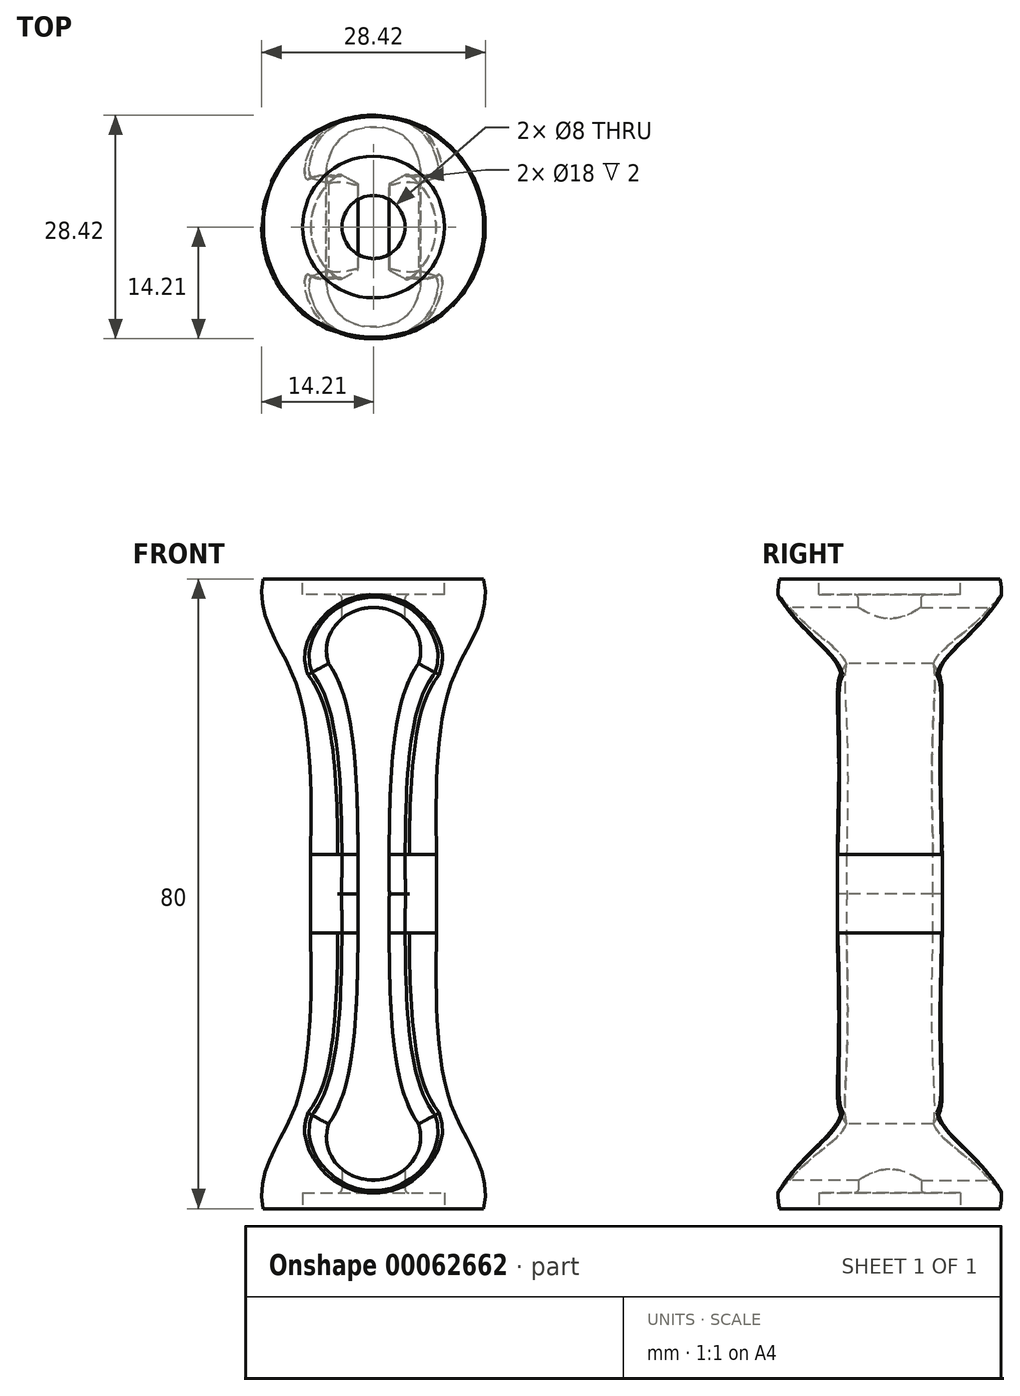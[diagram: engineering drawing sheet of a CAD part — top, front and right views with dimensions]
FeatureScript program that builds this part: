
annotation { "Feature Type Name" : "Feature", "Feature Type Description" : "" }
export const myFeature = defineFeature(function(context is Context, id is Id, definition is map)
    precondition{}
    {
        {
            var Q0;
            Q0=qCreatedBy(makeId("Front.planeOp"),FACE);
            var sketch = newSketch(context, id + "F0", { "sketchPlane" : qUnion([Q0])});
            skLineSegment(sketch, "E0", {"start": v(0, 0) * mm, "end": v(0, 40) * mm});
            skLineSegment(sketch, "E1", {"start": v(0, 40) * mm, "end": v(-14, 40) * mm});
            skLineSegment(sketch, "E2", {"start": v(0, 0) * mm, "end": v(-8, 0) * mm});
            skLineSegment(sketch, "E3", {"start": v(-8, 0) * mm, "end": v(-8, 5) * mm});
            skFitSpline(sketch, "E4", {"points": [v(-14, 40) * mm, v(-9.89, 26.85) * mm, v(-8, 5) * mm], "startDerivative": vector(-7.29, -34.58) * mm, "endDerivative": vector(-0.37, -33.72) * mm});
            skLineSegment(sketch, "E5.MirrorCS", {"start": v(-8, 0) * mm, "end": v(-8, -5) * mm});
            skLineSegment(sketch, "E6.MirrorCS", {"start": v(0, -40) * mm, "end": v(-14, -40) * mm});
            skLineSegment(sketch, "E7.MirrorCS", {"start": v(0, 0) * mm, "end": v(0, -40) * mm});
            skFitSpline(sketch, "E8.MirrorCS", {"points": [v(-14, -40) * mm, v(-9.89, -26.85) * mm, v(-8, -5) * mm], "startDerivative": vector(-7.29, 34.58) * mm, "endDerivative": vector(-0.37, 33.72) * mm});
            skSolve(sketch);
        }
        {
            var Q0;
            Q0 = qSketchRegion(id + "F0", true);
            var Q1;
            Q1=sQuery(id+"F0.wireOp",EDGE,"E7.MirrorCS");
            revolve(context, id + "F1", {"entities" : qUnion([Q0]), "axis" : qUnion([Q1]), "revolveType" : RevolveType.FULL});
        }
        {
            var Q0;
            Q0=makeQuery(id+"F1.opRevolve","SWEPT_FACE",FACE,{"disambiguationData":[OSD([sQuery(id+"F0.wireOp",EDGE,"E6.MirrorCS")])]});
            var sketch = newSketch(context, id + "F2", { "sketchPlane" : qUnion([Q0])});
            skCircle(sketch, "E9", {"center": v(0, 0) * mm, "radius": 4 * mm});
            skSolve(sketch);
        }
        {
            var Q0;
            Q0 = qSketchRegion(id + "F2", true);
            extrude(context, id + "F3", {"entities" : qUnion([Q0]), "operationType" : NewBodyOperationType.REMOVE, "oppositeDirection" : true, "depth" : 10 * mm});
        }
        {
            var Q0;
            Q0=qCreatedBy(makeId("Front.planeOp"),FACE);
            var sketch = newSketch(context, id + "F4", { "sketchPlane" : qUnion([Q0])});
            skLineSegment(sketch, "E10", {"start": v(0, 0) * mm, "end": v(0, 30.88) * mm});
            skLineSegment(sketch, "E11", {"start": v(2, 0) * mm, "end": v(-2, 0) * mm});
            skEllipticalArc(sketch, "E12", {});
            skFitSpline(sketch, "E13", {"points": [v(2, 0) * mm, v(5.72, 29.23) * mm, v(14.35, 33.66) * mm], "startDerivative": vector(-0.3, 57.22) * mm, "endDerivative": vector(24.53, 8.63) * mm});
            skLineSegment(sketch, "E14", {"start": v(0, 36.38) * mm, "end": v(0, 30.88) * mm});
            skEllipticalArc(sketch, "E15.MirrorCS", {});
            skFitSpline(sketch, "E16.MirrorCS", {"points": [v(-2, 0) * mm, v(-5.72, 29.23) * mm, v(-14.35, 33.66) * mm], "startDerivative": vector(0.3, 57.22) * mm, "endDerivative": vector(-24.53, 8.63) * mm});
            skFitSpline(sketch, "E17.MirrorCS", {"points": [v(2, 0) * mm, v(5.72, -29.23) * mm, v(14.35, -33.66) * mm], "startDerivative": vector(-0.3, -57.22) * mm, "endDerivative": vector(24.53, -8.63) * mm});
            skFitSpline(sketch, "E18.MirrorCS", {"points": [v(-2, 0) * mm, v(-5.72, -29.23) * mm, v(-14.35, -33.66) * mm], "startDerivative": vector(0.3, -57.22) * mm, "endDerivative": vector(-24.53, -8.63) * mm});
            skEllipticalArc(sketch, "E19.MirrorCS", {});
            skEllipticalArc(sketch, "E20.MirrorCS", {});
            const initialGuessF4  = {"E12": [0, 0.030878746884994077, 1, 0, 0.006, 0.0055, 5.978786873267516, 1.5707963267948966], "E15.MirrorCS": [0, 0.030878746884994077, -1, 0, 0.006, 0.0055, 4.71238898038469, 0.304398433912071], "E19.MirrorCS": [0, -0.030878746884994077, -1, 0, 0.006, 0.0055, 5.978786873267516, 1.5707963267948966], "E20.MirrorCS": [0, -0.030878746884994077, 1, 0, 0.006, 0.0055, 4.71238898038469, 0.3043984339120717]};
            skSetInitialGuess(sketch, initialGuessF4);
            skSolve(sketch);
        }
        {
            var Q0;
            Q0 = qSketchRegion(id + "F4", true);
            extrude(context, id + "F5", {"entities" : qUnion([Q0]), "operationType" : NewBodyOperationType.REMOVE, "endBound" : BoundingType.THROUGH_ALL, "oppositeDirection" : true, "depth" : 25 * mm, "hasSecondDirection" : true, "secondDirectionOppositeDirection" : false, "secondDirectionDepth" : 25 * mm});
        }
        {
            var Q0;
            Q0=makeQuery(id+"F1.opRevolve","SWEPT_FACE",FACE,{"disambiguationData":[OSD([sQuery(id+"F0.wireOp",EDGE,"E1")])]});
            var sketch = newSketch(context, id + "F6", { "sketchPlane" : qUnion([Q0])});
            skCircle(sketch, "E21", {"center": v(0, 0) * mm, "radius": 4 * mm});
            skSolve(sketch);
        }
        {
            var Q0;
            Q0 = qSketchRegion(id + "F6", true);
            extrude(context, id + "F7", {"entities" : qUnion([Q0]), "operationType" : NewBodyOperationType.REMOVE, "oppositeDirection" : true, "depth" : 10 * mm});
        }
        {
            var Q0;
            Q0=makeQuery(id+"F1.opRevolve","SWEPT_FACE",FACE,{"disambiguationData":[OSD([sQuery(id+"F0.wireOp",EDGE,"E6.MirrorCS")])]});
            var sketch = newSketch(context, id + "F8", { "sketchPlane" : qUnion([Q0])});
            skCircle(sketch, "E22", {"center": v(0, 0) * mm, "radius": 9 * mm});
            skSolve(sketch);
        }
        {
            var Q0;
            Q0 = qSketchRegion(id + "F8", true);
            extrude(context, id + "F9", {"entities" : qUnion([Q0]), "operationType" : NewBodyOperationType.REMOVE, "oppositeDirection" : true, "depth" : 2 * mm});
        }
        {
            var Q0;
            Q0=makeQuery(id+"F1.opRevolve","SWEPT_FACE",FACE,{"disambiguationData":[OSD([sQuery(id+"F0.wireOp",EDGE,"E1")])]});
            var sketch = newSketch(context, id + "F10", { "sketchPlane" : qUnion([Q0])});
            skCircle(sketch, "E23", {"center": v(0, 0) * mm, "radius": 9 * mm});
            skSolve(sketch);
        }
        {
            var Q0;
            Q0 = qSketchRegion(id + "F10", true);
            extrude(context, id + "F11", {"entities" : qUnion([Q0]), "operationType" : NewBodyOperationType.REMOVE, "oppositeDirection" : true, "depth" : 2 * mm});
        }
        {
            var Q0;
            Q0=makeQuery(id+"F5.boolean.opBoolean","INTERSECT",EDGE,{"disambiguationData":[OD(1.0)],"derivedFrom":[makeQuery(id+"F1.opRevolve","SWEPT_FACE",FACE,{"disambiguationData":[OSD([sQuery(id+"F0.wireOp",EDGE,"E8.MirrorCS")])]}),makeQuery(id+"F5.opExtrude","SWEPT_FACE",FACE,{"disambiguationData":[OSD([sQuery(id+"F4.wireOp",EDGE,"E19.MirrorCS"),sQuery(id+"F4.wireOp",EDGE,"E20.MirrorCS")])]})]});
            var Q1;
            Q1=makeQuery(id+"F5.boolean.opBoolean","INTERSECT",EDGE,{"disambiguationData":[OD(1.0)],"derivedFrom":[makeQuery(id+"F1.opRevolve","SWEPT_FACE",FACE,{"disambiguationData":[OSD([sQuery(id+"F0.wireOp",EDGE,"E8.MirrorCS")])]}),makeQuery(id+"F5.opExtrude","SWEPT_FACE",FACE,{"disambiguationData":[OSD([sQuery(id+"F4.wireOp",EDGE,"E17.MirrorCS")])]})]});
            var Q2;
            Q2=makeQuery(id+"F5.boolean.opBoolean","INTERSECT",EDGE,{"disambiguationData":[OD(1.0)],"derivedFrom":[makeQuery(id+"F1.opRevolve","SWEPT_FACE",FACE,{"disambiguationData":[OSD([sQuery(id+"F0.wireOp",EDGE,"E8.MirrorCS")])]}),makeQuery(id+"F5.opExtrude","SWEPT_FACE",FACE,{"disambiguationData":[OSD([sQuery(id+"F4.wireOp",EDGE,"E18.MirrorCS")])]})]});
            var Q3;
            Q3=makeQuery(id+"F5.boolean.opBoolean","INTERSECT",EDGE,{"disambiguationData":[OD(1.0)],"derivedFrom":[makeQuery(id+"F1.opRevolve","SWEPT_FACE",FACE,{"disambiguationData":[OSD([sQuery(id+"F0.wireOp",EDGE,"E3"),sQuery(id+"F0.wireOp",EDGE,"E5.MirrorCS")])]}),makeQuery(id+"F5.opExtrude","SWEPT_FACE",FACE,{"disambiguationData":[OSD([sQuery(id+"F4.wireOp",EDGE,"E18.MirrorCS")])]})]});
            var Q4;
            Q4=makeQuery(id+"F5.boolean.opBoolean","INTERSECT",EDGE,{"disambiguationData":[OD(1.0)],"derivedFrom":[makeQuery(id+"F1.opRevolve","SWEPT_FACE",FACE,{"disambiguationData":[OSD([sQuery(id+"F0.wireOp",EDGE,"E8.MirrorCS")])]}),makeQuery(id+"F5.opExtrude","SWEPT_FACE",FACE,{"disambiguationData":[OSD([sQuery(id+"F4.wireOp",EDGE,"E18.MirrorCS")])]})]});
            var Q5;
            Q5=makeQuery(id+"F5.boolean.opBoolean","INTERSECT",EDGE,{"disambiguationData":[OD(1.0)],"derivedFrom":[makeQuery(id+"F1.opRevolve","SWEPT_FACE",FACE,{"disambiguationData":[OSD([sQuery(id+"F0.wireOp",EDGE,"E3"),sQuery(id+"F0.wireOp",EDGE,"E5.MirrorCS")])]}),makeQuery(id+"F5.opExtrude","SWEPT_FACE",FACE,{"disambiguationData":[OSD([sQuery(id+"F4.wireOp",EDGE,"E17.MirrorCS")])]})]});
            var Q6;
            Q6=makeQuery(id+"F5.boolean.opBoolean","INTERSECT",EDGE,{"disambiguationData":[OD(1.0)],"derivedFrom":[makeQuery(id+"F1.opRevolve","SWEPT_FACE",FACE,{"disambiguationData":[OSD([sQuery(id+"F0.wireOp",EDGE,"E3"),sQuery(id+"F0.wireOp",EDGE,"E5.MirrorCS")])]}),makeQuery(id+"F5.opExtrude","SWEPT_FACE",FACE,{"disambiguationData":[OSD([sQuery(id+"F4.wireOp",EDGE,"E13")])]})]});
            var Q7;
            Q7=makeQuery(id+"F5.boolean.opBoolean","INTERSECT",EDGE,{"disambiguationData":[OD(1.0)],"derivedFrom":[makeQuery(id+"F1.opRevolve","SWEPT_FACE",FACE,{"disambiguationData":[OSD([sQuery(id+"F0.wireOp",EDGE,"E3"),sQuery(id+"F0.wireOp",EDGE,"E5.MirrorCS")])]}),makeQuery(id+"F5.opExtrude","SWEPT_FACE",FACE,{"disambiguationData":[OSD([sQuery(id+"F4.wireOp",EDGE,"E16.MirrorCS")])]})]});
            var Q8;
            Q8=makeQuery(id+"F5.boolean.opBoolean","INTERSECT",EDGE,{"disambiguationData":[OD(1.0)],"derivedFrom":[makeQuery(id+"F1.opRevolve","SWEPT_FACE",FACE,{"disambiguationData":[OSD([sQuery(id+"F0.wireOp",EDGE,"E4")])]}),makeQuery(id+"F5.opExtrude","SWEPT_FACE",FACE,{"disambiguationData":[OSD([sQuery(id+"F4.wireOp",EDGE,"E13")])]})]});
            var Q9;
            Q9=makeQuery(id+"F5.boolean.opBoolean","INTERSECT",EDGE,{"disambiguationData":[OD(1.0)],"derivedFrom":[makeQuery(id+"F1.opRevolve","SWEPT_FACE",FACE,{"disambiguationData":[OSD([sQuery(id+"F0.wireOp",EDGE,"E4")])]}),makeQuery(id+"F5.opExtrude","SWEPT_FACE",FACE,{"disambiguationData":[OSD([sQuery(id+"F4.wireOp",EDGE,"E16.MirrorCS")])]})]});
            var Q10;
            Q10=makeQuery(id+"F5.boolean.opBoolean","INTERSECT",EDGE,{"disambiguationData":[OD(1.0)],"derivedFrom":[makeQuery(id+"F1.opRevolve","SWEPT_FACE",FACE,{"disambiguationData":[OSD([sQuery(id+"F0.wireOp",EDGE,"E4")])]}),makeQuery(id+"F5.opExtrude","SWEPT_FACE",FACE,{"disambiguationData":[OSD([sQuery(id+"F4.wireOp",EDGE,"E12"),sQuery(id+"F4.wireOp",EDGE,"E15.MirrorCS")])]})]});
            var Q11;
            Q11=makeQuery(id+"F5.boolean.opBoolean","INTERSECT",EDGE,{"disambiguationData":[OD(0.0)],"derivedFrom":[makeQuery(id+"F1.opRevolve","SWEPT_FACE",FACE,{"disambiguationData":[OSD([sQuery(id+"F0.wireOp",EDGE,"E4")])]}),makeQuery(id+"F5.opExtrude","SWEPT_FACE",FACE,{"disambiguationData":[OSD([sQuery(id+"F4.wireOp",EDGE,"E13")])]})]});
            var Q12;
            Q12=makeQuery(id+"F5.boolean.opBoolean","INTERSECT",EDGE,{"disambiguationData":[OD(0.0)],"derivedFrom":[makeQuery(id+"F1.opRevolve","SWEPT_FACE",FACE,{"disambiguationData":[OSD([sQuery(id+"F0.wireOp",EDGE,"E4")])]}),makeQuery(id+"F5.opExtrude","SWEPT_FACE",FACE,{"disambiguationData":[OSD([sQuery(id+"F4.wireOp",EDGE,"E12"),sQuery(id+"F4.wireOp",EDGE,"E15.MirrorCS")])]})]});
            var Q13;
            Q13=makeQuery(id+"F5.boolean.opBoolean","INTERSECT",EDGE,{"disambiguationData":[OD(0.0)],"derivedFrom":[makeQuery(id+"F1.opRevolve","SWEPT_FACE",FACE,{"disambiguationData":[OSD([sQuery(id+"F0.wireOp",EDGE,"E4")])]}),makeQuery(id+"F5.opExtrude","SWEPT_FACE",FACE,{"disambiguationData":[OSD([sQuery(id+"F4.wireOp",EDGE,"E16.MirrorCS")])]})]});
            var Q14;
            Q14=makeQuery(id+"F5.boolean.opBoolean","INTERSECT",EDGE,{"disambiguationData":[OD(0.0)],"derivedFrom":[makeQuery(id+"F1.opRevolve","SWEPT_FACE",FACE,{"disambiguationData":[OSD([sQuery(id+"F0.wireOp",EDGE,"E3"),sQuery(id+"F0.wireOp",EDGE,"E5.MirrorCS")])]}),makeQuery(id+"F5.opExtrude","SWEPT_FACE",FACE,{"disambiguationData":[OSD([sQuery(id+"F4.wireOp",EDGE,"E13")])]})]});
            var Q15;
            Q15=makeQuery(id+"F5.boolean.opBoolean","INTERSECT",EDGE,{"disambiguationData":[OD(0.0)],"derivedFrom":[makeQuery(id+"F1.opRevolve","SWEPT_FACE",FACE,{"disambiguationData":[OSD([sQuery(id+"F0.wireOp",EDGE,"E3"),sQuery(id+"F0.wireOp",EDGE,"E5.MirrorCS")])]}),makeQuery(id+"F5.opExtrude","SWEPT_FACE",FACE,{"disambiguationData":[OSD([sQuery(id+"F4.wireOp",EDGE,"E17.MirrorCS")])]})]});
            var Q16;
            Q16=makeQuery(id+"F5.boolean.opBoolean","INTERSECT",EDGE,{"disambiguationData":[OD(0.0)],"derivedFrom":[makeQuery(id+"F1.opRevolve","SWEPT_FACE",FACE,{"disambiguationData":[OSD([sQuery(id+"F0.wireOp",EDGE,"E3"),sQuery(id+"F0.wireOp",EDGE,"E5.MirrorCS")])]}),makeQuery(id+"F5.opExtrude","SWEPT_FACE",FACE,{"disambiguationData":[OSD([sQuery(id+"F4.wireOp",EDGE,"E16.MirrorCS")])]})]});
            var Q17;
            Q17=makeQuery(id+"F5.boolean.opBoolean","INTERSECT",EDGE,{"disambiguationData":[OD(0.0)],"derivedFrom":[makeQuery(id+"F1.opRevolve","SWEPT_FACE",FACE,{"disambiguationData":[OSD([sQuery(id+"F0.wireOp",EDGE,"E3"),sQuery(id+"F0.wireOp",EDGE,"E5.MirrorCS")])]}),makeQuery(id+"F5.opExtrude","SWEPT_FACE",FACE,{"disambiguationData":[OSD([sQuery(id+"F4.wireOp",EDGE,"E18.MirrorCS")])]})]});
            var Q18;
            Q18=makeQuery(id+"F5.boolean.opBoolean","INTERSECT",EDGE,{"disambiguationData":[OD(0.0)],"derivedFrom":[makeQuery(id+"F1.opRevolve","SWEPT_FACE",FACE,{"disambiguationData":[OSD([sQuery(id+"F0.wireOp",EDGE,"E8.MirrorCS")])]}),makeQuery(id+"F5.opExtrude","SWEPT_FACE",FACE,{"disambiguationData":[OSD([sQuery(id+"F4.wireOp",EDGE,"E17.MirrorCS")])]})]});
            var Q19;
            Q19=makeQuery(id+"F5.boolean.opBoolean","INTERSECT",EDGE,{"disambiguationData":[OD(0.0)],"derivedFrom":[makeQuery(id+"F1.opRevolve","SWEPT_FACE",FACE,{"disambiguationData":[OSD([sQuery(id+"F0.wireOp",EDGE,"E3"),sQuery(id+"F0.wireOp",EDGE,"E5.MirrorCS")])]}),makeQuery(id+"F5.opExtrude","SWEPT_FACE",FACE,{"disambiguationData":[OSD([sQuery(id+"F4.wireOp",EDGE,"E18.MirrorCS")])]})]});
            var Q20;
            Q20=makeQuery(id+"F5.boolean.opBoolean","INTERSECT",EDGE,{"disambiguationData":[OD(0.0)],"derivedFrom":[makeQuery(id+"F1.opRevolve","SWEPT_FACE",FACE,{"disambiguationData":[OSD([sQuery(id+"F0.wireOp",EDGE,"E8.MirrorCS")])]}),makeQuery(id+"F5.opExtrude","SWEPT_FACE",FACE,{"disambiguationData":[OSD([sQuery(id+"F4.wireOp",EDGE,"E18.MirrorCS")])]})]});
            var Q21;
            Q21=makeQuery(id+"F5.boolean.opBoolean","INTERSECT",EDGE,{"disambiguationData":[OD(0.0)],"derivedFrom":[makeQuery(id+"F1.opRevolve","SWEPT_FACE",FACE,{"disambiguationData":[OSD([sQuery(id+"F0.wireOp",EDGE,"E8.MirrorCS")])]}),makeQuery(id+"F5.opExtrude","SWEPT_FACE",FACE,{"disambiguationData":[OSD([sQuery(id+"F4.wireOp",EDGE,"E19.MirrorCS"),sQuery(id+"F4.wireOp",EDGE,"E20.MirrorCS")])]})]});
            chamfer(context, id + "F12", {"entities" : qUnion([Q0, Q1, Q2, Q3, Q4, Q5, Q6, Q7, Q8, Q9, Q10, Q11, Q12, Q13, Q14, Q15, Q16, Q17, Q18, Q19, Q20, Q21]), "width" : 1.5 * mm, "tangentPropagation" : true});
        }
        {
            var Q0;
            {var subQ0=makeQuery(id+"F1.opRevolve","SWEPT_FACE",FACE,{"disambiguationData":[OSD([sQuery(id+"F0.wireOp",EDGE,"E8.MirrorCS")])]});Q0=makeQuery(id+"F12.opChamfer","BLEND_EDGE",EDGE,{"blendedFrom":[makeQuery(id+"F5.boolean.opBoolean","INTERSECT",EDGE,{"disambiguationData":[OD(0.0)],"derivedFrom":[subQ0,makeQuery(id+"F5.opExtrude","SWEPT_FACE",FACE,{"disambiguationData":[OSD([sQuery(id+"F4.wireOp",EDGE,"E19.MirrorCS"),sQuery(id+"F4.wireOp",EDGE,"E20.MirrorCS")])]})]}),subQ0],"blendedInto":[subQ0]});}
            var Q1;
            {var subQ0=makeQuery(id+"F1.opRevolve","SWEPT_FACE",FACE,{"disambiguationData":[OSD([sQuery(id+"F0.wireOp",EDGE,"E8.MirrorCS")])]});Q1=makeQuery(id+"F12.opChamfer","BLEND_EDGE",EDGE,{"blendedFrom":[makeQuery(id+"F5.boolean.opBoolean","INTERSECT",EDGE,{"disambiguationData":[OD(0.0)],"derivedFrom":[subQ0,makeQuery(id+"F5.opExtrude","SWEPT_FACE",FACE,{"disambiguationData":[OSD([sQuery(id+"F4.wireOp",EDGE,"E18.MirrorCS")])]})]}),subQ0],"blendedInto":[subQ0]});}
            var Q2;
            {var subQ0=makeQuery(id+"F1.opRevolve","SWEPT_FACE",FACE,{"disambiguationData":[OSD([sQuery(id+"F0.wireOp",EDGE,"E8.MirrorCS")])]});Q2=makeQuery(id+"F12.opChamfer","BLEND_EDGE",EDGE,{"blendedFrom":[makeQuery(id+"F5.boolean.opBoolean","INTERSECT",EDGE,{"disambiguationData":[OD(0.0)],"derivedFrom":[subQ0,makeQuery(id+"F5.opExtrude","SWEPT_FACE",FACE,{"disambiguationData":[OSD([sQuery(id+"F4.wireOp",EDGE,"E17.MirrorCS")])]})]}),subQ0],"blendedInto":[subQ0]});}
            var Q3;
            {var subQ0=makeQuery(id+"F5.opExtrude","SWEPT_FACE",FACE,{"disambiguationData":[OSD([sQuery(id+"F4.wireOp",EDGE,"E18.MirrorCS")])]});var subQ1=makeQuery(id+"F1.opRevolve","SWEPT_FACE",FACE,{"disambiguationData":[OSD([sQuery(id+"F0.wireOp",EDGE,"E3"),sQuery(id+"F0.wireOp",EDGE,"E5.MirrorCS")])]});Q3=makeQuery(id+"F12.opChamfer","BLEND_EDGE",EDGE,{"blendedFrom":[makeQuery(id+"F5.boolean.opBoolean","INTERSECT",EDGE,{"disambiguationData":[OD(0.0)],"derivedFrom":[subQ1,subQ0]}),makeQuery(id+"F5.boolean.opBoolean","SPLIT",FACE,{"disambiguationData":[TD([makeQuery(id+"F5.opExtrude","SWEPT_FACE",FACE,{"disambiguationData":[OSD([sQuery(id+"F4.wireOp",EDGE,"E16.MirrorCS")])]})])],"derivedFrom":subQ1})],"blendedInto":[makeQuery(id+"F5.boolean.opBoolean","SPLIT",FACE,{"disambiguationData":[TD([makeQuery(id+"F5.opExtrude","SWEPT_FACE",FACE,{"disambiguationData":[OSD([sQuery(id+"F4.wireOp",EDGE,"E16.MirrorCS")])]})])],"derivedFrom":subQ1})]});}
            var Q4;
            {var subQ0=makeQuery(id+"F5.opExtrude","SWEPT_FACE",FACE,{"disambiguationData":[OSD([sQuery(id+"F4.wireOp",EDGE,"E16.MirrorCS")])]});var subQ1=makeQuery(id+"F1.opRevolve","SWEPT_FACE",FACE,{"disambiguationData":[OSD([sQuery(id+"F0.wireOp",EDGE,"E3"),sQuery(id+"F0.wireOp",EDGE,"E5.MirrorCS")])]});Q4=makeQuery(id+"F12.opChamfer","BLEND_EDGE",EDGE,{"blendedFrom":[makeQuery(id+"F5.boolean.opBoolean","INTERSECT",EDGE,{"disambiguationData":[OD(0.0)],"derivedFrom":[subQ1,subQ0]}),makeQuery(id+"F5.boolean.opBoolean","SPLIT",FACE,{"disambiguationData":[TD([subQ0])],"derivedFrom":subQ1})],"blendedInto":[makeQuery(id+"F5.boolean.opBoolean","SPLIT",FACE,{"disambiguationData":[TD([subQ0])],"derivedFrom":subQ1})]});}
            var Q5;
            {var subQ0=makeQuery(id+"F1.opRevolve","SWEPT_FACE",FACE,{"disambiguationData":[OSD([sQuery(id+"F0.wireOp",EDGE,"E4")])]});Q5=makeQuery(id+"F12.opChamfer","BLEND_EDGE",EDGE,{"blendedFrom":[makeQuery(id+"F5.boolean.opBoolean","INTERSECT",EDGE,{"disambiguationData":[OD(0.0)],"derivedFrom":[subQ0,makeQuery(id+"F5.opExtrude","SWEPT_FACE",FACE,{"disambiguationData":[OSD([sQuery(id+"F4.wireOp",EDGE,"E16.MirrorCS")])]})]}),subQ0],"blendedInto":[subQ0]});}
            var Q6;
            {var subQ0=makeQuery(id+"F1.opRevolve","SWEPT_FACE",FACE,{"disambiguationData":[OSD([sQuery(id+"F0.wireOp",EDGE,"E4")])]});Q6=makeQuery(id+"F12.opChamfer","BLEND_EDGE",EDGE,{"blendedFrom":[makeQuery(id+"F5.boolean.opBoolean","INTERSECT",EDGE,{"disambiguationData":[OD(0.0)],"derivedFrom":[subQ0,makeQuery(id+"F5.opExtrude","SWEPT_FACE",FACE,{"disambiguationData":[OSD([sQuery(id+"F4.wireOp",EDGE,"E12"),sQuery(id+"F4.wireOp",EDGE,"E15.MirrorCS")])]})]}),subQ0],"blendedInto":[subQ0]});}
            var Q7;
            {var subQ0=makeQuery(id+"F1.opRevolve","SWEPT_FACE",FACE,{"disambiguationData":[OSD([sQuery(id+"F0.wireOp",EDGE,"E4")])]});Q7=makeQuery(id+"F12.opChamfer","BLEND_EDGE",EDGE,{"blendedFrom":[makeQuery(id+"F5.boolean.opBoolean","INTERSECT",EDGE,{"disambiguationData":[OD(0.0)],"derivedFrom":[subQ0,makeQuery(id+"F5.opExtrude","SWEPT_FACE",FACE,{"disambiguationData":[OSD([sQuery(id+"F4.wireOp",EDGE,"E13")])]})]}),subQ0],"blendedInto":[subQ0]});}
            var Q8;
            {var subQ0=makeQuery(id+"F5.opExtrude","SWEPT_FACE",FACE,{"disambiguationData":[OSD([sQuery(id+"F4.wireOp",EDGE,"E13")])]});var subQ1=makeQuery(id+"F1.opRevolve","SWEPT_FACE",FACE,{"disambiguationData":[OSD([sQuery(id+"F0.wireOp",EDGE,"E3"),sQuery(id+"F0.wireOp",EDGE,"E5.MirrorCS")])]});Q8=makeQuery(id+"F12.opChamfer","BLEND_EDGE",EDGE,{"blendedFrom":[makeQuery(id+"F5.boolean.opBoolean","INTERSECT",EDGE,{"disambiguationData":[OD(0.0)],"derivedFrom":[subQ1,subQ0]}),makeQuery(id+"F5.boolean.opBoolean","SPLIT",FACE,{"disambiguationData":[TD([subQ0])],"derivedFrom":subQ1})],"blendedInto":[makeQuery(id+"F5.boolean.opBoolean","SPLIT",FACE,{"disambiguationData":[TD([subQ0])],"derivedFrom":subQ1})]});}
            var Q9;
            {var subQ0=makeQuery(id+"F5.opExtrude","SWEPT_FACE",FACE,{"disambiguationData":[OSD([sQuery(id+"F4.wireOp",EDGE,"E17.MirrorCS")])]});var subQ1=makeQuery(id+"F1.opRevolve","SWEPT_FACE",FACE,{"disambiguationData":[OSD([sQuery(id+"F0.wireOp",EDGE,"E3"),sQuery(id+"F0.wireOp",EDGE,"E5.MirrorCS")])]});Q9=makeQuery(id+"F12.opChamfer","BLEND_EDGE",EDGE,{"blendedFrom":[makeQuery(id+"F5.boolean.opBoolean","INTERSECT",EDGE,{"disambiguationData":[OD(0.0)],"derivedFrom":[subQ1,subQ0]}),makeQuery(id+"F5.boolean.opBoolean","SPLIT",FACE,{"disambiguationData":[TD([makeQuery(id+"F5.opExtrude","SWEPT_FACE",FACE,{"disambiguationData":[OSD([sQuery(id+"F4.wireOp",EDGE,"E13")])]})])],"derivedFrom":subQ1})],"blendedInto":[makeQuery(id+"F5.boolean.opBoolean","SPLIT",FACE,{"disambiguationData":[TD([makeQuery(id+"F5.opExtrude","SWEPT_FACE",FACE,{"disambiguationData":[OSD([sQuery(id+"F4.wireOp",EDGE,"E13")])]})])],"derivedFrom":subQ1})]});}
            var Q10;
            {var subQ0=makeQuery(id+"F1.opRevolve","SWEPT_FACE",FACE,{"disambiguationData":[OSD([sQuery(id+"F0.wireOp",EDGE,"E4")])]});Q10=makeQuery(id+"F12.opChamfer","BLEND_EDGE",EDGE,{"blendedFrom":[makeQuery(id+"F5.boolean.opBoolean","INTERSECT",EDGE,{"disambiguationData":[OD(1.0)],"derivedFrom":[subQ0,makeQuery(id+"F5.opExtrude","SWEPT_FACE",FACE,{"disambiguationData":[OSD([sQuery(id+"F4.wireOp",EDGE,"E12"),sQuery(id+"F4.wireOp",EDGE,"E15.MirrorCS")])]})]}),subQ0],"blendedInto":[subQ0]});}
            var Q11;
            {var subQ0=makeQuery(id+"F1.opRevolve","SWEPT_FACE",FACE,{"disambiguationData":[OSD([sQuery(id+"F0.wireOp",EDGE,"E4")])]});Q11=makeQuery(id+"F12.opChamfer","BLEND_EDGE",EDGE,{"blendedFrom":[makeQuery(id+"F5.boolean.opBoolean","INTERSECT",EDGE,{"disambiguationData":[OD(1.0)],"derivedFrom":[subQ0,makeQuery(id+"F5.opExtrude","SWEPT_FACE",FACE,{"disambiguationData":[OSD([sQuery(id+"F4.wireOp",EDGE,"E13")])]})]}),subQ0],"blendedInto":[subQ0]});}
            var Q12;
            {var subQ0=makeQuery(id+"F1.opRevolve","SWEPT_FACE",FACE,{"disambiguationData":[OSD([sQuery(id+"F0.wireOp",EDGE,"E4")])]});Q12=makeQuery(id+"F12.opChamfer","BLEND_EDGE",EDGE,{"blendedFrom":[makeQuery(id+"F5.boolean.opBoolean","INTERSECT",EDGE,{"disambiguationData":[OD(1.0)],"derivedFrom":[subQ0,makeQuery(id+"F5.opExtrude","SWEPT_FACE",FACE,{"disambiguationData":[OSD([sQuery(id+"F4.wireOp",EDGE,"E16.MirrorCS")])]})]}),subQ0],"blendedInto":[subQ0]});}
            var Q13;
            {var subQ0=makeQuery(id+"F5.opExtrude","SWEPT_FACE",FACE,{"disambiguationData":[OSD([sQuery(id+"F4.wireOp",EDGE,"E16.MirrorCS")])]});var subQ1=makeQuery(id+"F1.opRevolve","SWEPT_FACE",FACE,{"disambiguationData":[OSD([sQuery(id+"F0.wireOp",EDGE,"E3"),sQuery(id+"F0.wireOp",EDGE,"E5.MirrorCS")])]});Q13=makeQuery(id+"F12.opChamfer","BLEND_EDGE",EDGE,{"blendedFrom":[makeQuery(id+"F5.boolean.opBoolean","INTERSECT",EDGE,{"disambiguationData":[OD(1.0)],"derivedFrom":[subQ1,subQ0]}),makeQuery(id+"F5.boolean.opBoolean","SPLIT",FACE,{"disambiguationData":[TD([subQ0])],"derivedFrom":subQ1})],"blendedInto":[makeQuery(id+"F5.boolean.opBoolean","SPLIT",FACE,{"disambiguationData":[TD([subQ0])],"derivedFrom":subQ1})]});}
            var Q14;
            {var subQ0=makeQuery(id+"F5.opExtrude","SWEPT_FACE",FACE,{"disambiguationData":[OSD([sQuery(id+"F4.wireOp",EDGE,"E18.MirrorCS")])]});var subQ1=makeQuery(id+"F1.opRevolve","SWEPT_FACE",FACE,{"disambiguationData":[OSD([sQuery(id+"F0.wireOp",EDGE,"E3"),sQuery(id+"F0.wireOp",EDGE,"E5.MirrorCS")])]});Q14=makeQuery(id+"F12.opChamfer","BLEND_EDGE",EDGE,{"blendedFrom":[makeQuery(id+"F5.boolean.opBoolean","INTERSECT",EDGE,{"disambiguationData":[OD(1.0)],"derivedFrom":[subQ1,subQ0]}),makeQuery(id+"F5.boolean.opBoolean","SPLIT",FACE,{"disambiguationData":[TD([makeQuery(id+"F5.opExtrude","SWEPT_FACE",FACE,{"disambiguationData":[OSD([sQuery(id+"F4.wireOp",EDGE,"E16.MirrorCS")])]})])],"derivedFrom":subQ1})],"blendedInto":[makeQuery(id+"F5.boolean.opBoolean","SPLIT",FACE,{"disambiguationData":[TD([makeQuery(id+"F5.opExtrude","SWEPT_FACE",FACE,{"disambiguationData":[OSD([sQuery(id+"F4.wireOp",EDGE,"E16.MirrorCS")])]})])],"derivedFrom":subQ1})]});}
            var Q15;
            {var subQ0=makeQuery(id+"F5.opExtrude","SWEPT_FACE",FACE,{"disambiguationData":[OSD([sQuery(id+"F4.wireOp",EDGE,"E13")])]});var subQ1=makeQuery(id+"F1.opRevolve","SWEPT_FACE",FACE,{"disambiguationData":[OSD([sQuery(id+"F0.wireOp",EDGE,"E3"),sQuery(id+"F0.wireOp",EDGE,"E5.MirrorCS")])]});Q15=makeQuery(id+"F12.opChamfer","BLEND_EDGE",EDGE,{"blendedFrom":[makeQuery(id+"F5.boolean.opBoolean","INTERSECT",EDGE,{"disambiguationData":[OD(1.0)],"derivedFrom":[subQ1,subQ0]}),makeQuery(id+"F5.boolean.opBoolean","SPLIT",FACE,{"disambiguationData":[TD([subQ0])],"derivedFrom":subQ1})],"blendedInto":[makeQuery(id+"F5.boolean.opBoolean","SPLIT",FACE,{"disambiguationData":[TD([subQ0])],"derivedFrom":subQ1})]});}
            var Q16;
            {var subQ0=makeQuery(id+"F5.opExtrude","SWEPT_FACE",FACE,{"disambiguationData":[OSD([sQuery(id+"F4.wireOp",EDGE,"E17.MirrorCS")])]});var subQ1=makeQuery(id+"F1.opRevolve","SWEPT_FACE",FACE,{"disambiguationData":[OSD([sQuery(id+"F0.wireOp",EDGE,"E3"),sQuery(id+"F0.wireOp",EDGE,"E5.MirrorCS")])]});Q16=makeQuery(id+"F12.opChamfer","BLEND_EDGE",EDGE,{"blendedFrom":[makeQuery(id+"F5.boolean.opBoolean","INTERSECT",EDGE,{"disambiguationData":[OD(1.0)],"derivedFrom":[subQ1,subQ0]}),makeQuery(id+"F5.boolean.opBoolean","SPLIT",FACE,{"disambiguationData":[TD([makeQuery(id+"F5.opExtrude","SWEPT_FACE",FACE,{"disambiguationData":[OSD([sQuery(id+"F4.wireOp",EDGE,"E13")])]})])],"derivedFrom":subQ1})],"blendedInto":[makeQuery(id+"F5.boolean.opBoolean","SPLIT",FACE,{"disambiguationData":[TD([makeQuery(id+"F5.opExtrude","SWEPT_FACE",FACE,{"disambiguationData":[OSD([sQuery(id+"F4.wireOp",EDGE,"E13")])]})])],"derivedFrom":subQ1})]});}
            var Q17;
            {var subQ0=makeQuery(id+"F1.opRevolve","SWEPT_FACE",FACE,{"disambiguationData":[OSD([sQuery(id+"F0.wireOp",EDGE,"E8.MirrorCS")])]});Q17=makeQuery(id+"F12.opChamfer","BLEND_EDGE",EDGE,{"blendedFrom":[makeQuery(id+"F5.boolean.opBoolean","INTERSECT",EDGE,{"disambiguationData":[OD(1.0)],"derivedFrom":[subQ0,makeQuery(id+"F5.opExtrude","SWEPT_FACE",FACE,{"disambiguationData":[OSD([sQuery(id+"F4.wireOp",EDGE,"E17.MirrorCS")])]})]}),subQ0],"blendedInto":[subQ0]});}
            var Q18;
            {var subQ0=makeQuery(id+"F1.opRevolve","SWEPT_FACE",FACE,{"disambiguationData":[OSD([sQuery(id+"F0.wireOp",EDGE,"E8.MirrorCS")])]});Q18=makeQuery(id+"F12.opChamfer","BLEND_EDGE",EDGE,{"blendedFrom":[makeQuery(id+"F5.boolean.opBoolean","INTERSECT",EDGE,{"disambiguationData":[OD(1.0)],"derivedFrom":[subQ0,makeQuery(id+"F5.opExtrude","SWEPT_FACE",FACE,{"disambiguationData":[OSD([sQuery(id+"F4.wireOp",EDGE,"E18.MirrorCS")])]})]}),subQ0],"blendedInto":[subQ0]});}
            var Q19;
            {var subQ0=makeQuery(id+"F1.opRevolve","SWEPT_FACE",FACE,{"disambiguationData":[OSD([sQuery(id+"F0.wireOp",EDGE,"E8.MirrorCS")])]});Q19=makeQuery(id+"F12.opChamfer","BLEND_EDGE",EDGE,{"blendedFrom":[makeQuery(id+"F5.boolean.opBoolean","INTERSECT",EDGE,{"disambiguationData":[OD(1.0)],"derivedFrom":[subQ0,makeQuery(id+"F5.opExtrude","SWEPT_FACE",FACE,{"disambiguationData":[OSD([sQuery(id+"F4.wireOp",EDGE,"E19.MirrorCS"),sQuery(id+"F4.wireOp",EDGE,"E20.MirrorCS")])]})]}),subQ0],"blendedInto":[subQ0]});}
            fillet(context, id + "F13", {"entities" : qUnion([Q0, Q1, Q2, Q3, Q4, Q5, Q6, Q7, Q8, Q9, Q10, Q11, Q12, Q13, Q14, Q15, Q16, Q17, Q18, Q19]), "radius" : .5 * mm, "tangentPropagation" : true, "allowEdgeOverflow" : false});
        }
        {
            var Q0;
            Q0=makeQuery(id+"F9.boolean.opBoolean","COPY",EDGE,{"derivedFrom":makeQuery(id+"F9.opExtrude","CAP_EDGE",EDGE,{"disambiguationData":[OSD([sQuery(id+"F8.wireOp",EDGE,"E22")])],"isStart":true})});
            var Q1;
            Q1=makeQuery(id+"F9.boolean.opBoolean","INTERSECT",EDGE,{"derivedFrom":[makeQuery(id+"F3.boolean.opBoolean","COPY",FACE,{"derivedFrom":makeQuery(id+"F3.opExtrude","SWEPT_FACE",FACE,{"disambiguationData":[OSD([sQuery(id+"F2.wireOp",EDGE,"E9")])]})}),makeQuery(id+"F9.opExtrude","CAP_FACE",FACE,{"disambiguationData":[OSD([sQuery(id+"F8.wireOp",EDGE,"E22")])],"isStart":false})]});
            var Q2;
            Q2=makeQuery(id+"F11.boolean.opBoolean","COPY",EDGE,{"derivedFrom":makeQuery(id+"F11.opExtrude","CAP_EDGE",EDGE,{"disambiguationData":[OSD([sQuery(id+"F10.wireOp",EDGE,"E23")])],"isStart":true})});
            var Q3;
            Q3=makeQuery(id+"F11.boolean.opBoolean","INTERSECT",EDGE,{"derivedFrom":[makeQuery(id+"F7.boolean.opBoolean","COPY",FACE,{"derivedFrom":makeQuery(id+"F7.opExtrude","SWEPT_FACE",FACE,{"disambiguationData":[OSD([sQuery(id+"F6.wireOp",EDGE,"E21")])]})}),makeQuery(id+"F11.opExtrude","CAP_FACE",FACE,{"disambiguationData":[OSD([sQuery(id+"F10.wireOp",EDGE,"E23")])],"isStart":false})]});
            fillet(context, id + "F14", {"entities" : qUnion([Q0, Q1, Q2, Q3]), "radius" : .5 * mm, "tangentPropagation" : true, "allowEdgeOverflow" : false});
        }
    });
